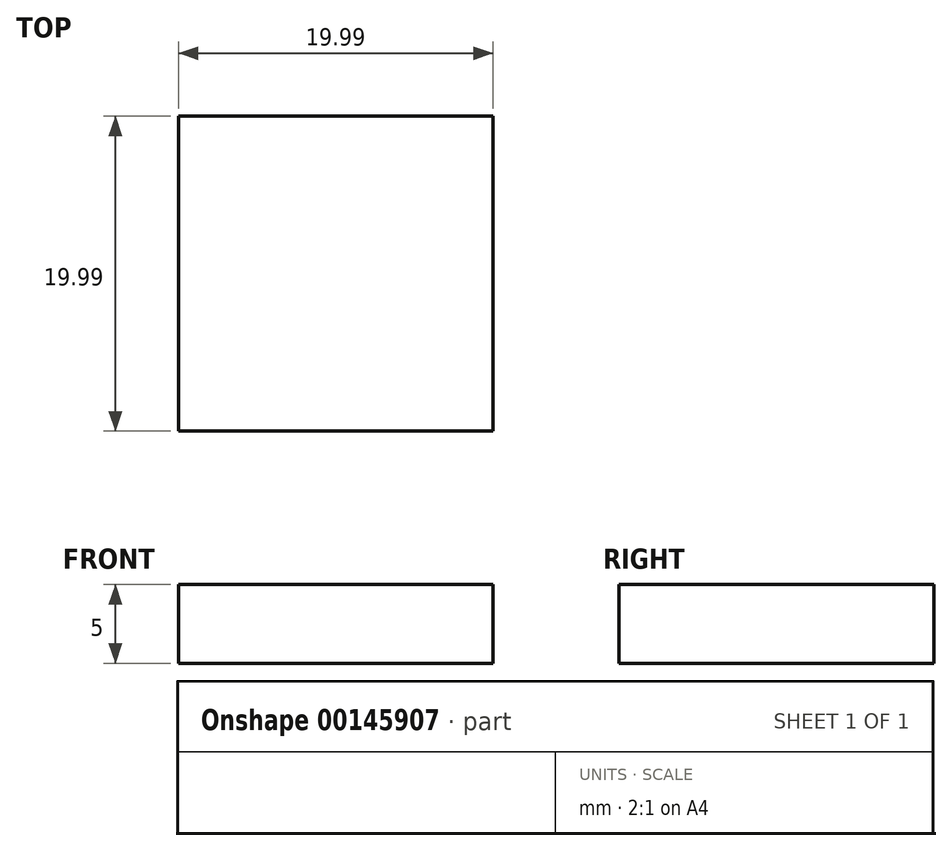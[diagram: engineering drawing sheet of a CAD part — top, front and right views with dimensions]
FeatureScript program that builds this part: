
annotation { "Feature Type Name" : "Feature", "Feature Type Description" : "" }
export const myFeature = defineFeature(function(context is Context, id is Id, definition is map)
    precondition{}
    {
        {
            var Q0;
            Q0=qCreatedBy(makeId("Top.planeOp"),FACE);
            var sketch = newSketch(context, id + "F0", { "sketchPlane" : qUnion([Q0])});
            skLineSegment(sketch, "E0.bottom", {"start": v(0, 0) * mm, "end": v(19.99, 0) * mm});
            skLineSegment(sketch, "E0.top", {"start": v(0, -19.99) * mm, "end": v(19.99, -19.99) * mm});
            skLineSegment(sketch, "E0.left", {"start": v(0, 0) * mm, "end": v(0, -19.99) * mm});
            skLineSegment(sketch, "E0.right", {"start": v(19.99, 0) * mm, "end": v(19.99, -19.99) * mm});
            skSolve(sketch);
        }
        {
            var Q0;
            Q0 = qSketchRegion(id + "F0", true);
            extrude(context, id + "F1", {"entities" : qUnion([Q0]), "depth" : 5 * mm});
        }
    });
